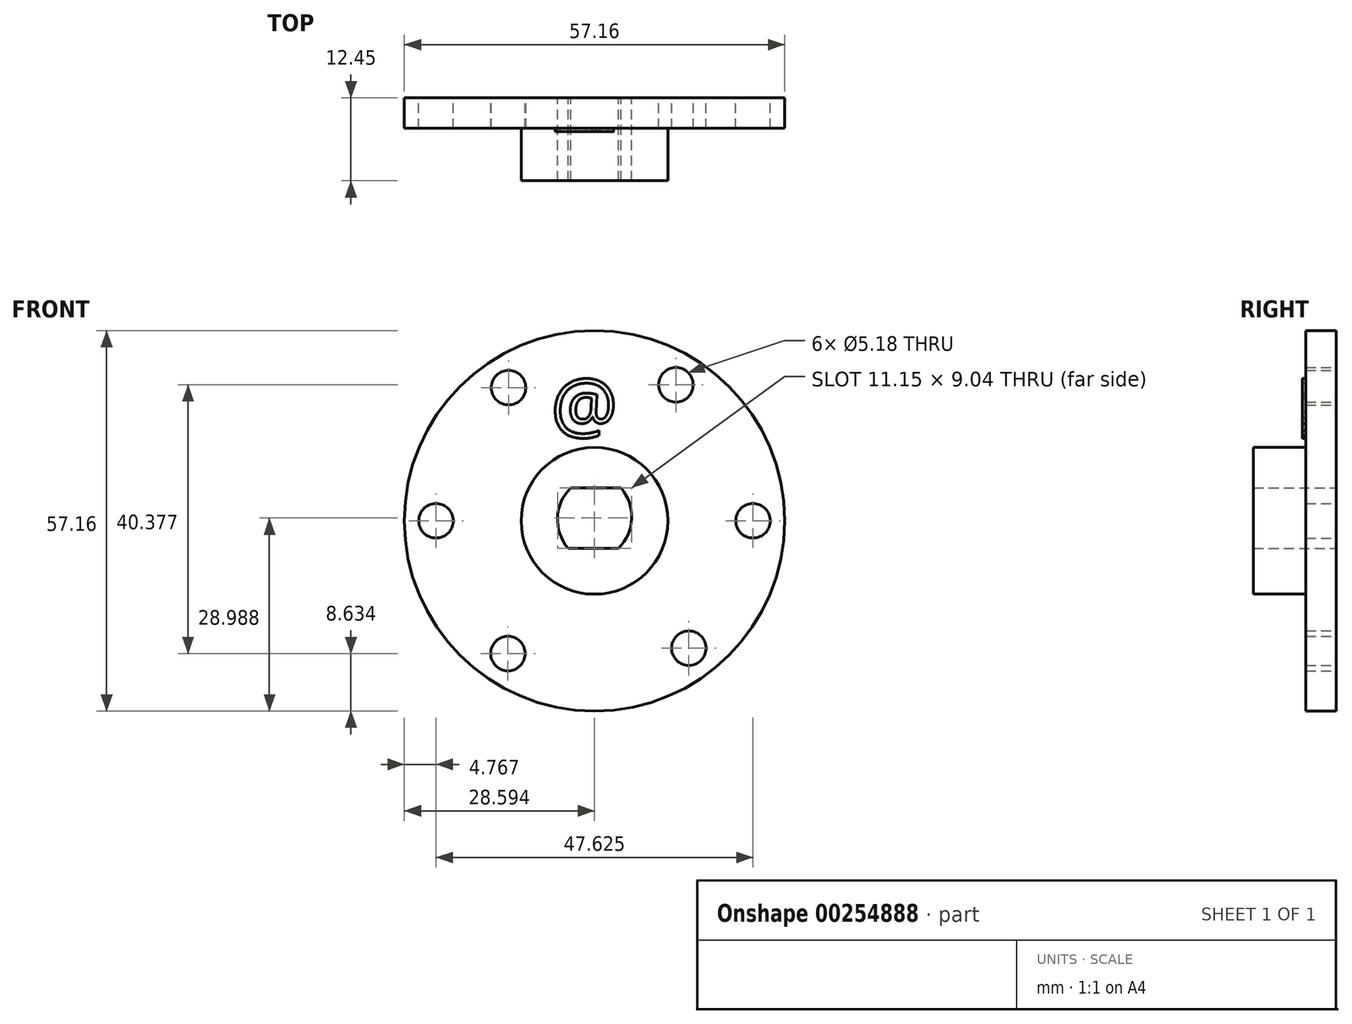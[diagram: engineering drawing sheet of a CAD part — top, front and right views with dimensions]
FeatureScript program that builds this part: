
annotation { "Feature Type Name" : "Feature", "Feature Type Description" : "" }
export const myFeature = defineFeature(function(context is Context, id is Id, definition is map)
    precondition{}
    {
        {
            var Q0;
            Q0=qCreatedBy(makeId("Front.planeOp"),FACE);
            var sketch = newSketch(context, id + "F0", { "sketchPlane" : qUnion([Q0])});
            skCircle(sketch, "E0", {"center": v(0, 0) * mm, "radius": 28.58 * mm});
            skCircle(sketch, "E1", {"center": v(12.23, 20.43) * mm, "radius": 2.6 * mm});
            skCircle(sketch, "E2", {"center": v(23.81, 0) * mm, "radius": 2.6 * mm});
            skCircle(sketch, "E3", {"center": v(14.17, -19.14) * mm, "radius": 2.6 * mm});
            skCircle(sketch, "E4", {"center": v(-13, -19.95) * mm, "radius": 2.6 * mm});
            skCircle(sketch, "E5", {"center": v(-23.81, 0) * mm, "radius": 2.6 * mm});
            skCircle(sketch, "E6", {"center": v(-12.91, 20) * mm, "radius": 2.6 * mm});
            skCircle(sketch, "E7", {"center": v(0, 0) * mm, "radius": 11.02 * mm});
            skLineSegment(sketch, "E8", {"start": v(-3.6, 4.93) * mm, "end": v(3.96, 4.93) * mm});
            skLineSegment(sketch, "E9", {"start": v(-3.98, -4.11) * mm, "end": v(3.58, -4.11) * mm});
            skArc(sketch, "E10", {"start": v(3.58, -4.11) * mm, "mid": v(5.59, 0.33) * mm, "end": v(3.96, 4.93) * mm});
            skArc(sketch, "E11", {"start": v(-3.6, 4.93) * mm, "mid": v(-5.56, 0.48) * mm, "end": v(-3.98, -4.11) * mm});
            skSolve(sketch);
        }
        {
            var Q0;
            Q0=makeQuery(id+"F0.imprint","IMPRINT",FACE,{"disambiguationData":[TD([[makeQuery(id+"F0.imprint","IMPRINT",EDGE,{"derivedFrom":sQuery(id+"F0.wireOp",EDGE,"E0")}),1.0]])]});
            extrude(context, id + "F1", {"entities" : qUnion([Q0]), "depth" : 4.57 * mm});
        }
        {
            var Q0;
            Q0=makeQuery(id+"F0.imprint","IMPRINT",FACE,{"disambiguationData":[TD([[makeQuery(id+"F0.imprint","IMPRINT",EDGE,{"derivedFrom":sQuery(id+"F0.wireOp",EDGE,"E7")}),1.0]])]});
            extrude(context, id + "F2", {"entities" : qUnion([Q0]), "operationType" : NewBodyOperationType.ADD, "depth" : 12.45 * mm});
        }
        {
            var Q0;
            Q0=qCreatedBy(makeId("Front.planeOp"),FACE);
            var sketch = newSketch(context, id + "F3", { "sketchPlane" : qUnion([Q0])});
            skText(sketch, "E12", { "text": "@", "fontName": "OpenSans-Regular.ttf"});
            const initialGuessF3  = {"E12": [-0.00657, 0.01339, 1, 0, 0.00807]};
            skSetInitialGuess(sketch, initialGuessF3);
            skSolve(sketch);
        }
        {
            var Q0;
            Q0 = qSketchRegion(id + "F3", true);
            extrude(context, id + "F4", {"entities" : qUnion([Q0]), "operationType" : NewBodyOperationType.ADD, "depth" : 5.08 * mm});
        }
    });
